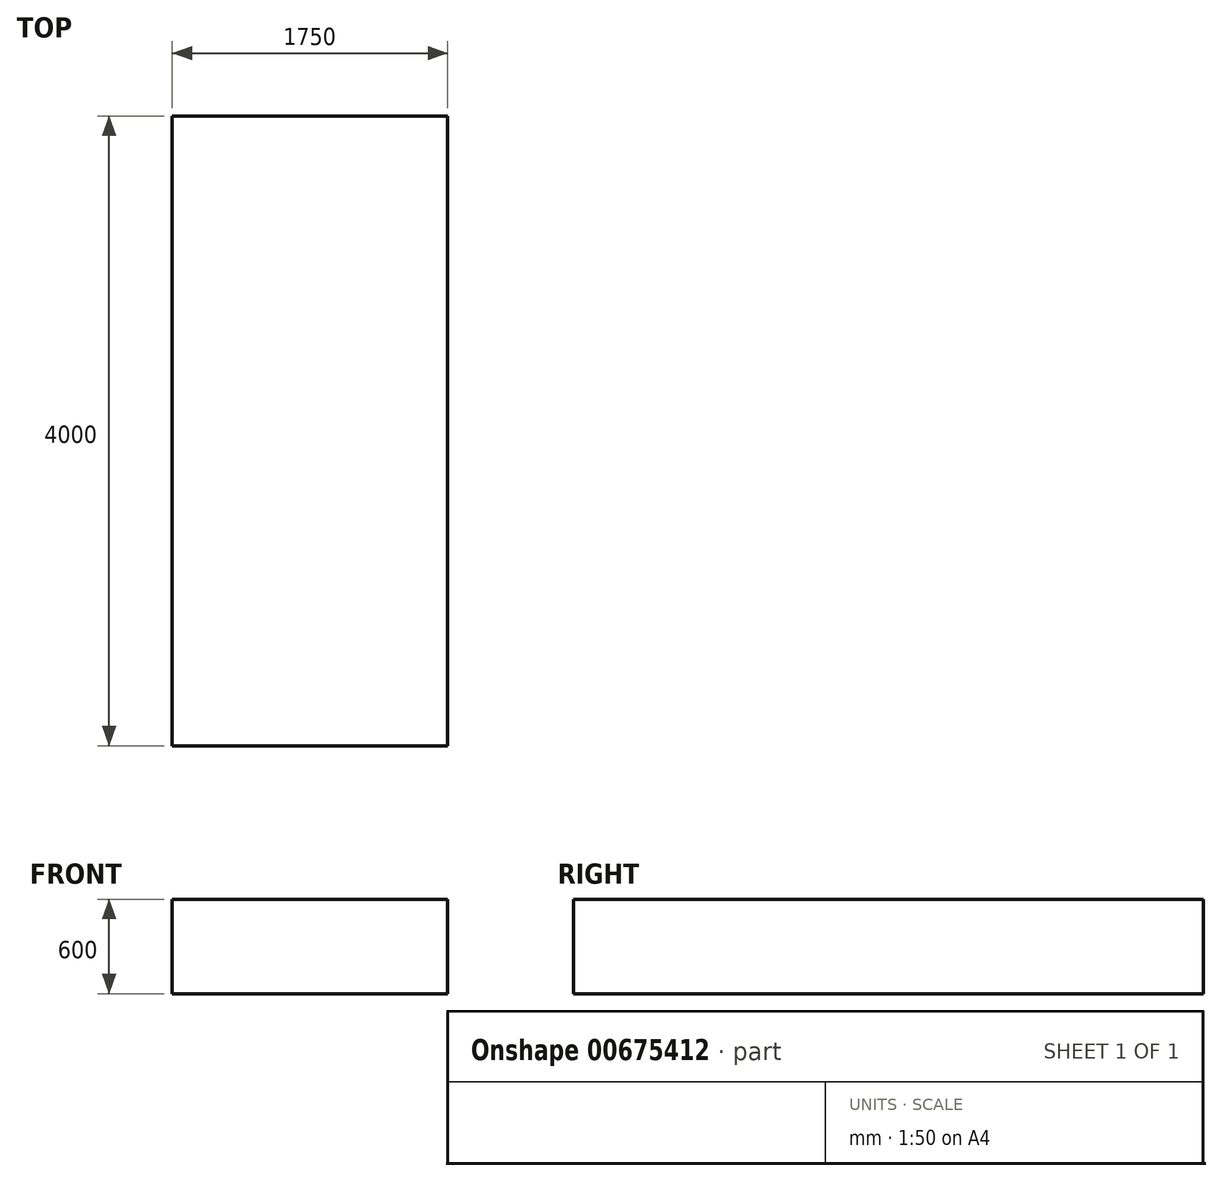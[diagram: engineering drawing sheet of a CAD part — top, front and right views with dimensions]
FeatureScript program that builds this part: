
annotation { "Feature Type Name" : "Feature", "Feature Type Description" : "" }
export const myFeature = defineFeature(function(context is Context, id is Id, definition is map)
    precondition{}
    {
        {
            var Q0;
            Q0=qCreatedBy(makeId("Front.planeOp"),FACE);
            var sketch = newSketch(context, id + "F0", { "sketchPlane" : qUnion([Q0])});
            skLineSegment(sketch, "E0.bottom", {"start": v(0, 0) * mm, "end": v(1750, 0) * mm});
            skLineSegment(sketch, "E0.top", {"start": v(0, 600) * mm, "end": v(1750, 600) * mm});
            skLineSegment(sketch, "E0.left", {"start": v(0, 0) * mm, "end": v(0, 600) * mm});
            skLineSegment(sketch, "E0.right", {"start": v(1750, 0) * mm, "end": v(1750, 600) * mm});
            skSolve(sketch);
        }
        {
            var Q0;
            Q0=qSketchRegion(id+"F0",true);
            extrude(context, id + "F1", {"entities" : qUnion([Q0]), "depth" : 4000 * mm, "offsetDistance" : 25 * mm});
        }
    });
